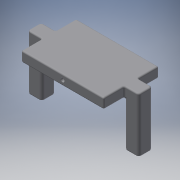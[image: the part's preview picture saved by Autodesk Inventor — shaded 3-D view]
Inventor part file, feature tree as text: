
AUTODESK INVENTOR PART (.ipt)
format: ipt  version: 2018 (Build 220112000, 112)  size: 306,176 bytes
history: native  units: mm
features: other x6, fillet x5, extrude x4, sketch x4, reference x4
ambient origin geometry x8: Origin, YZ Plane, XZ Plane, XY Plane, X Axis, Y Axis, Z Axis, Center Point
bodies: Solid1 (feature_tree)
feature tree (23):
  extrude  "Extrusion1"  Depth=5.0mm
  extrude  "Extrusion2"  Depth=10.5mm
  fillet  "Fillet1"  Radius=40.0mm
  fillet  "Fillet2"  Radius=2.0mm
  fillet  "Fillet3"  Radius=1.0mm
  fillet  "Fillet4"  Radius=1.0mm
  fillet  "Fillet5"  Radius=1.0mm
  extrude  "Extrusion3"  Depth=1.0mm
  extrude  "Extrusion4"  Depth=8.0mm
  sketch  "Sketch1"  dims[d0=7.5mm d1=0.0mm d2=5.0mm]
  reference  "Reference1"
  sketch  "Sketch2"  dims[d3=10.0mm d4=10.5mm d5=40.0mm d6=0.0mm d7=2.0mm d8=1.0mm d9=1.0mm d10=1.0mm]
  reference  "Reference2"
  reference  "Reference3"
  sketch  "Sketch3"  dims[d11=1.0mm d12=2.8mm]
  reference  "Reference4"
  sketch  "Sketch4"  dims[d13=8.0mm d14=0.0mm d15=2.8mm d16=8.0mm d17=0.0mm]
  other  "<userpath>\OneDrive\Documents\Inventor\TSA\2018\Animatronics\Tortoise\TurtleAssembly2.iam"
  other  "TurtleAssembly2.iam"
  other  "ButtonMount:1"
  other  "<userpath>\OneDrive\Documents\Inventor\TSA\2018\Animatronics\Tortoise\Turtle3.iam"
  other  "Turtle3.iam"
  other  "ButtonLockerV2:1"
